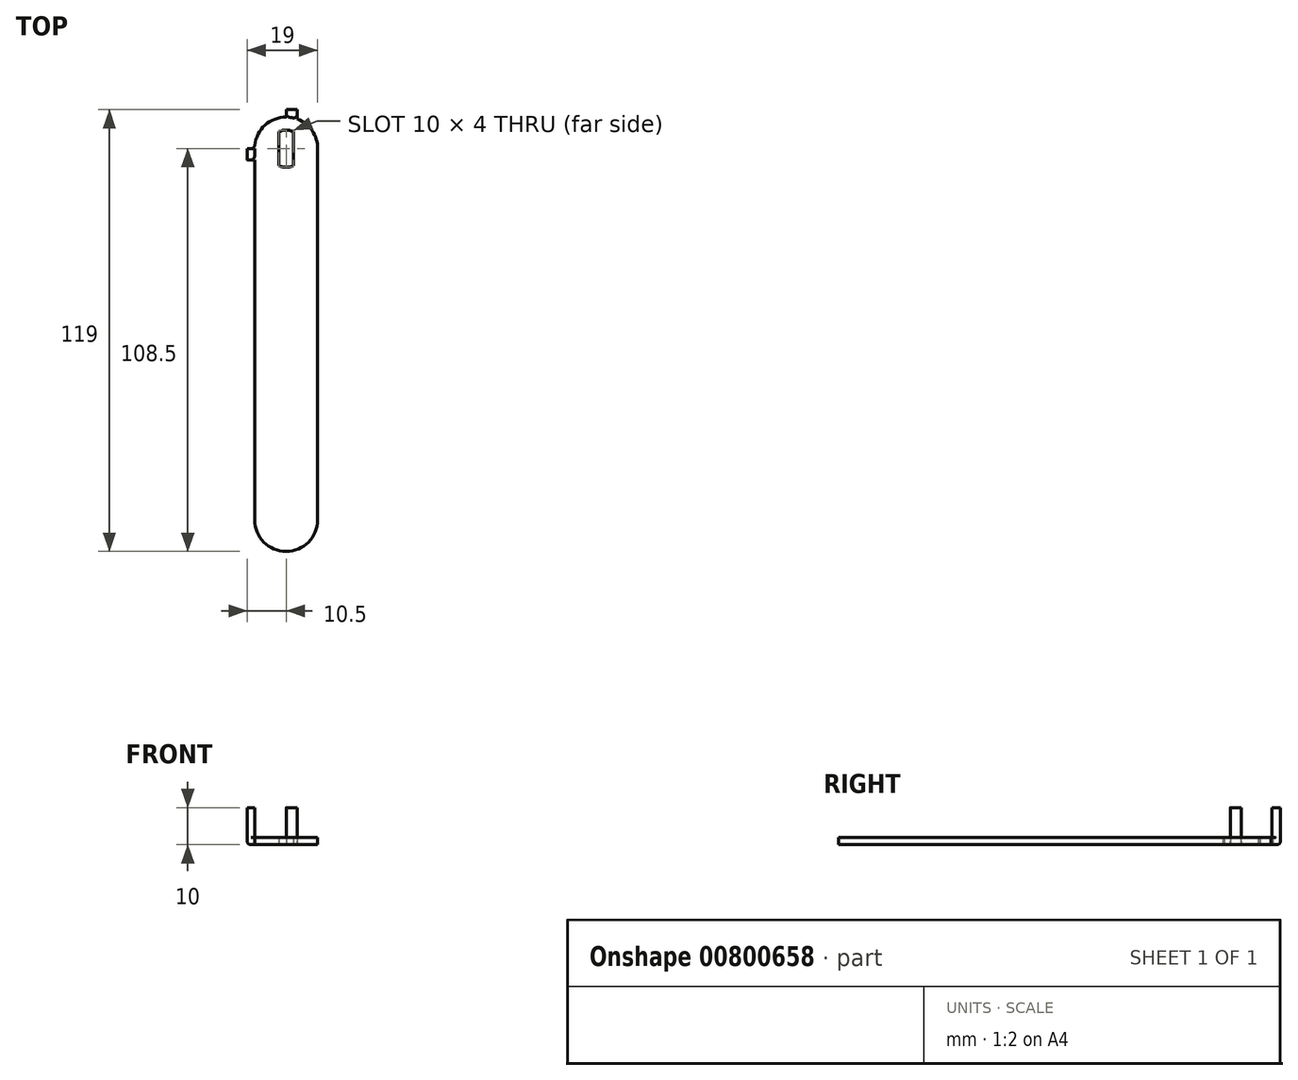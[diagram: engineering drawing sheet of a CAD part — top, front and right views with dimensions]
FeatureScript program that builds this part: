
annotation { "Feature Type Name" : "Feature", "Feature Type Description" : "" }
export const myFeature = defineFeature(function(context is Context, id is Id, definition is map)
    precondition{}
    {
        {
            var Q0;
            Q0=qCreatedBy(makeId("Top.planeOp"),FACE);
            var sketch = newSketch(context, id + "F0", { "sketchPlane" : qUnion([Q0])});
            skArc(sketch, "E0", {"start": v(8.5, 0) * mm, "mid": v(0, 8.5) * mm, "end": v(-8.5, 0) * mm});
            skLineSegment(sketch, "E1", {"start": v(-8.5, 0) * mm, "end": v(-8.5, -100) * mm});
            skLineSegment(sketch, "E2", {"start": v(8.5, 0) * mm, "end": v(8.5, -100) * mm});
            skArc(sketch, "E3", {"start": v(-8.5, -100) * mm, "mid": v(0, -108.5) * mm, "end": v(8.5, -100) * mm});
            skArc(sketch, "E4", {"start": v(2, 4.58) * mm, "mid": v(0, 5) * mm, "end": v(-2, 4.58) * mm});
            skLineSegment(sketch, "E5", {"start": v(-2, 4.58) * mm, "end": v(-2, -4.58) * mm});
            skLineSegment(sketch, "E6", {"start": v(2, 4.58) * mm, "end": v(2, -4.58) * mm});
            skArc(sketch, "E7.trimOffspring", {"start": v(-2, -4.58) * mm, "mid": v(0, -5) * mm, "end": v(2, -4.58) * mm});
            skSolve(sketch);
        }
        {
            var Q0;
            Q0 = qSketchRegion(id + "F0", true);
            extrude(context, id + "F1", {"entities" : qUnion([Q0]), "depth" : 2 * mm, "offsetDistance" : 25 * mm});
        }
        {
            var Q0;
            Q0=qCreatedBy(makeId("Top.planeOp"),FACE);
            var sketch = newSketch(context, id + "F2", { "sketchPlane" : qUnion([Q0])});
            skLineSegment(sketch, "E8.0", {"start": v(-8.5, 0) * mm, "end": v(-8.5, -100) * mm, "construction": true});
            skArc(sketch, "E9.0", {"start": v(8.5, 0) * mm, "mid": v(0, 8.5) * mm, "end": v(-8.5, 0) * mm, "construction": true});
            skLineSegment(sketch, "E10.0", {"start": v(8.5, 0) * mm, "end": v(8.5, -100) * mm, "construction": true});
            skLineSegment(sketch, "E11", {"start": v(-8.5, 0) * mm, "end": v(-10.5, 0) * mm});
            skLineSegment(sketch, "E12", {"start": v(-10.5, 0) * mm, "end": v(-10.5, -3) * mm});
            skLineSegment(sketch, "E13", {"start": v(-10.5, -3) * mm, "end": v(-8.5, -3) * mm});
            skLineSegment(sketch, "E14", {"start": v(-8.5, -3) * mm, "end": v(-8.5, 0) * mm});
            skLineSegment(sketch, "E15", {"start": v(0, 8.5) * mm, "end": v(0, 10.5) * mm});
            skLineSegment(sketch, "E16", {"start": v(0, 10.5) * mm, "end": v(3, 10.5) * mm});
            skLineSegment(sketch, "E17", {"start": v(3, 10.5) * mm, "end": v(3, 7.95) * mm});
            skArc(sketch, "E18", {"start": v(3, 7.95) * mm, "mid": v(1.52, 8.36) * mm, "end": v(0, 8.5) * mm});
            skSolve(sketch);
        }
        {
            var Q0;
            Q0 = qSketchRegion(id + "F2", true);
            extrude(context, id + "F3", {"entities" : qUnion([Q0]), "operationType" : NewBodyOperationType.ADD, "depth" : 10 * mm, "offsetDistance" : 25 * mm});
        }
        {
            var Q0;
            Q0=makeQuery(id+"F3.boolean.opBoolean","MERGE",EDGE,{"derivedFrom":[makeQuery(id+"F1.opExtrude","SWEPT_EDGE",EDGE,{"disambiguationData":[OSD([sQuery(id+"F0.wireOp",EDGE,"E0"),sQuery(id+"F0.wireOp",EDGE,"E1")])]}),makeQuery(id+"F3.opExtrude","SWEPT_EDGE",EDGE,{"disambiguationData":[OSD([sQuery(id+"F2.wireOp",EDGE,"E11"),sQuery(id+"F2.wireOp",EDGE,"E14")])]})]});
            var Q1;
            {var subQ0=sQuery(id+"F2.wireOp",EDGE,"E15");Q1=makeQuery(id+"F3.boolean.opBoolean","SPLIT",EDGE,{"disambiguationData":[topologyDisambiguationEdgeConnected([makeQuery(id+"F1.opExtrude","SWEPT_FACE",FACE,{"disambiguationData":[OSD([sQuery(id+"F0.wireOp",EDGE,"E0")])]})])],"derivedFrom":makeQuery(id+"F3.opExtrude","SWEPT_EDGE",EDGE,{"disambiguationData":[OSD([subQ0,sQuery(id+"F2.wireOp",EDGE,"E18")])]})});}
            var Q2;
            {var subQ0=sQuery(id+"F2.wireOp",EDGE,"E13");Q2=makeQuery(id+"F3.boolean.opBoolean","SPLIT",EDGE,{"disambiguationData":[topologyDisambiguationEdgeConnected([makeQuery(id+"F1.opExtrude","SWEPT_FACE",FACE,{"disambiguationData":[OSD([sQuery(id+"F0.wireOp",EDGE,"E1")])]})])],"derivedFrom":makeQuery(id+"F3.opExtrude","SWEPT_EDGE",EDGE,{"disambiguationData":[OSD([subQ0,sQuery(id+"F2.wireOp",EDGE,"E14")])]})});}
            var Q3;
            {var subQ0=sQuery(id+"F2.wireOp",EDGE,"E17");Q3=makeQuery(id+"F3.boolean.opBoolean","SPLIT",EDGE,{"disambiguationData":[topologyDisambiguationEdgeConnected([makeQuery(id+"F1.opExtrude","SWEPT_FACE",FACE,{"disambiguationData":[OSD([sQuery(id+"F0.wireOp",EDGE,"E0")])]})])],"derivedFrom":makeQuery(id+"F3.opExtrude","SWEPT_EDGE",EDGE,{"disambiguationData":[OSD([subQ0,sQuery(id+"F2.wireOp",EDGE,"E18")])]})});}
            var Q4;
            Q4=makeQuery(id+"F3.opExtrude","CAP_EDGE",EDGE,{"disambiguationData":[OSD([sQuery(id+"F2.wireOp",EDGE,"E12")])],"isStart":true});
            var Q5;
            Q5=makeQuery(id+"F3.opExtrude","CAP_EDGE",EDGE,{"disambiguationData":[OSD([sQuery(id+"F2.wireOp",EDGE,"E16")])],"isStart":true});
            fillet(context, id + "F4", {"entities" : qUnion([Q0, Q1, Q2, Q3, Q4, Q5]), "radius" : 1 * mm, "tangentPropagation" : true, "allowEdgeOverflow" : false});
        }
    });
